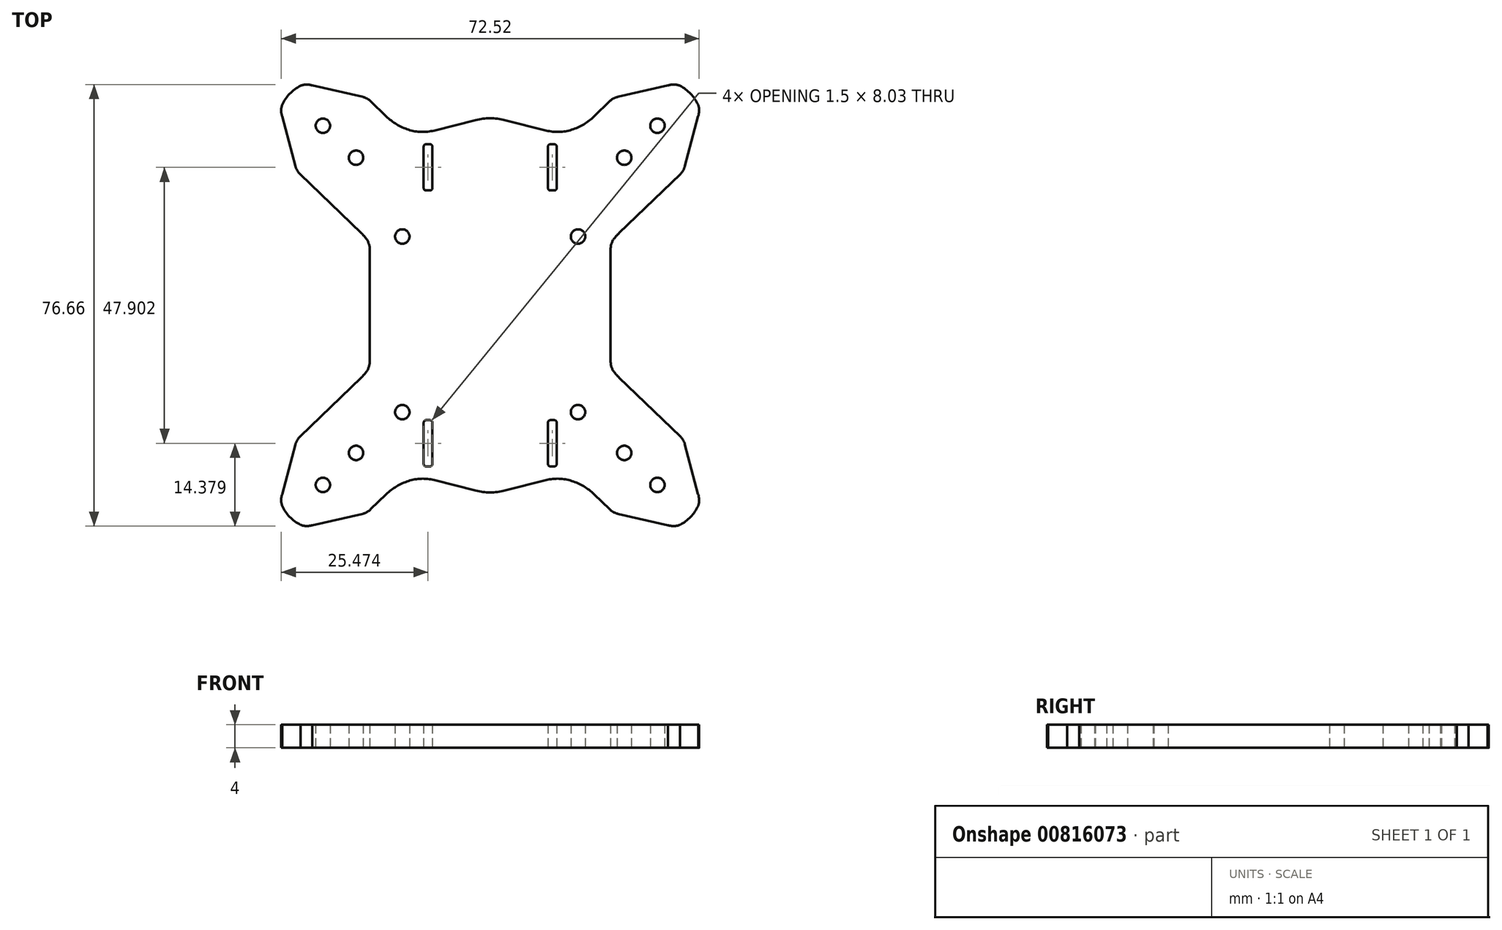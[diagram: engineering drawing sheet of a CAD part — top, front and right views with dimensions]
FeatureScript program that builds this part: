
annotation { "Feature Type Name" : "Feature", "Feature Type Description" : "" }
export const myFeature = defineFeature(function(context is Context, id is Id, definition is map)
    precondition{}
    {
        {
            var Q0;
            Q0=qCreatedBy(makeId("Top.planeOp"),FACE);
            var sketch = newSketch(context, id + "F0", { "sketchPlane" : qUnion([Q0])});
            skArc(sketch, "E0.filletArc", {"start": v(22.37, 12.53) * mm, "mid": v(21.96, 12.11) * mm, "end": v(21.58, 11.68) * mm});
            skArc(sketch, "E1.MirrorCS", {"start": v(18.04, 32.81) * mm, "mid": v(16.23, 31.43) * mm, "end": v(14.16, 30.49) * mm});
            skArc(sketch, "E2.MirrorCS", {"start": v(32.98, 22.77) * mm, "mid": v(33.49, 23.41) * mm, "end": v(33.8, 24.17) * mm});
            skLineSegment(sketch, "E3.MirrorCS", {"start": v(20, 34.7) * mm, "end": v(18.04, 32.81) * mm});
            skLineSegment(sketch, "E4.MirrorCS", {"start": v(20, 34.7) * mm, "end": v(20.76, 35.44) * mm});
            skLineSegment(sketch, "E5.MirrorCS", {"start": v(25.58, 36.97) * mm, "end": v(22.18, 36.2) * mm});
            skArc(sketch, "E6.MirrorCS", {"start": v(36.09, 34.84) * mm, "mid": v(36.26, 33.8) * mm, "end": v(36.07, 32.77) * mm});
            skArc(sketch, "E7.MirrorCS", {"start": v(32.93, 38.11) * mm, "mid": v(31.9, 38.32) * mm, "end": v(30.86, 38.17) * mm});
            skLineSegment(sketch, "E8.MirrorCS", {"start": v(34.69, 27.53) * mm, "end": v(33.8, 24.17) * mm});
            skArc(sketch, "E9.MirrorCS", {"start": v(22.18, 36.2) * mm, "mid": v(21.42, 35.92) * mm, "end": v(20.76, 35.44) * mm});
            skArc(sketch, "E10.MirrorCS", {"start": v(36.09, 34.84) * mm, "mid": v(34.78, 36.74) * mm, "end": v(32.93, 38.11) * mm});
            skLineSegment(sketch, "E11.MirrorCS", {"start": v(30.86, 38.17) * mm, "end": v(25.58, 36.97) * mm});
            skLineSegment(sketch, "E12.MirrorCS", {"start": v(36.07, 32.77) * mm, "end": v(34.69, 27.53) * mm});
            skCircle(sketch, "E13.MirrorC", {"center": v(29.03, 31.18) * mm, "radius": 1.25 * mm});
            skCircle(sketch, "E14.MirrorC", {"center": v(23.27, 25.63) * mm, "radius": 1.25 * mm});
            skLineSegment(sketch, "E15.MirrorCS", {"start": v(32.98, 22.77) * mm, "end": v(22.37, 12.53) * mm});
            skLineSegment(sketch, "E16", {"start": v(2.5, 32.18) * mm, "end": v(9.75, 30.34) * mm});
            skArc(sketch, "E17.filletArc", {"start": v(9.75, 30.34) * mm, "mid": v(11.97, 30.1) * mm, "end": v(14.16, 30.49) * mm});
            skPoint(sketch, "E18.visualSharp", {"position": v(20.83, 7.15) * mm});
            skArc(sketch, "E18.filletArc", {"start": v(21.58, 11.68) * mm, "mid": v(21.08, 10.79) * mm, "end": v(20.9, 9.77) * mm});
            skLineSegment(sketch, "E19.bottom", {"start": v(10.04, 11.8) * mm, "end": v(-8.96, 11.8) * mm, "construction": true});
            skPoint(sketch, "E20", {"position": v(10.04, 24.6) * mm});
            skLineSegment(sketch, "E21.MirrorCS", {"start": v(10.04, 27.56) * mm, "end": v(10.04, 24.6) * mm});
            skLineSegment(sketch, "E22.MirrorCS", {"start": v(10.44, 27.96) * mm, "end": v(11.14, 27.96) * mm});
            skLineSegment(sketch, "E23.MirrorCS", {"start": v(11.54, 27.56) * mm, "end": v(11.54, 20.34) * mm});
            skLineSegment(sketch, "E24.MirrorCS", {"start": v(10.04, 24.6) * mm, "end": v(10.04, 20.34) * mm});
            skLineSegment(sketch, "E25.MirrorCS", {"start": v(10.44, 19.94) * mm, "end": v(11.14, 19.94) * mm});
            skPoint(sketch, "E26.visualSharp", {"position": v(11.54, 16.64) * mm});
            skArc(sketch, "E26.filletArc", {"start": v(11.14, 19.94) * mm, "mid": v(11.42, 20.05) * mm, "end": v(11.54, 20.34) * mm});
            skPoint(sketch, "E27.visualSharp", {"position": v(11.54, 27.96) * mm});
            skArc(sketch, "E27.filletArc", {"start": v(11.54, 27.56) * mm, "mid": v(11.42, 27.85) * mm, "end": v(11.14, 27.96) * mm});
            skPoint(sketch, "E28.visualSharp", {"position": v(10.04, 16.64) * mm});
            skArc(sketch, "E28.filletArc", {"start": v(10.04, 20.34) * mm, "mid": v(10.15, 20.05) * mm, "end": v(10.44, 19.94) * mm});
            skLineSegment(sketch, "E29.trimOffspring", {"start": v(10.04, 30.28) * mm, "end": v(10.04, 34.1) * mm, "construction": true});
            skPoint(sketch, "E30.MirrorCS.start.orphan", {"position": v(10.04, 27.96) * mm});
            skPoint(sketch, "E31.orphan", {"position": v(10.29, 8.83) * mm});
            skArc(sketch, "E32.filletArc", {"start": v(10.44, 27.96) * mm, "mid": v(10.15, 27.85) * mm, "end": v(10.04, 27.56) * mm});
            skLineSegment(sketch, "E33.MirrorCS", {"start": v(-10.44, 27.96) * mm, "end": v(-11.14, 27.96) * mm});
            skArc(sketch, "E34.MirrorCS", {"start": v(-11.54, 27.56) * mm, "mid": v(-11.42, 27.85) * mm, "end": v(-11.14, 27.96) * mm});
            skArc(sketch, "E35.MirrorCS", {"start": v(-10.44, 27.96) * mm, "mid": v(-10.15, 27.85) * mm, "end": v(-10.04, 27.56) * mm});
            skLineSegment(sketch, "E36.MirrorCS", {"start": v(-10.44, 19.94) * mm, "end": v(-11.14, 19.94) * mm});
            skArc(sketch, "E37.MirrorCS", {"start": v(-11.14, 19.94) * mm, "mid": v(-11.42, 20.05) * mm, "end": v(-11.54, 20.34) * mm});
            skArc(sketch, "E38.MirrorCS", {"start": v(-10.04, 20.34) * mm, "mid": v(-10.15, 20.05) * mm, "end": v(-10.44, 19.94) * mm});
            skLineSegment(sketch, "E39.MirrorCS", {"start": v(-10.04, 27.56) * mm, "end": v(-10.04, 24.6) * mm});
            skLineSegment(sketch, "E40.MirrorCS", {"start": v(-11.54, 27.56) * mm, "end": v(-11.54, 20.34) * mm});
            skLineSegment(sketch, "E41.MirrorCS", {"start": v(-10.04, 24.6) * mm, "end": v(-10.04, 20.34) * mm});
            skLineSegment(sketch, "E42.MirrorCS", {"start": v(-20, 34.7) * mm, "end": v(-18.04, 32.81) * mm});
            skLineSegment(sketch, "E43.MirrorCS", {"start": v(-34.69, 27.53) * mm, "end": v(-33.8, 24.17) * mm});
            skArc(sketch, "E44.MirrorCS", {"start": v(-32.98, 22.77) * mm, "mid": v(-33.49, 23.41) * mm, "end": v(-33.8, 24.17) * mm});
            skArc(sketch, "E45.MirrorCS", {"start": v(-9.75, 30.34) * mm, "mid": v(-11.97, 30.1) * mm, "end": v(-14.16, 30.49) * mm});
            skLineSegment(sketch, "E46.MirrorCS", {"start": v(-25.58, 36.97) * mm, "end": v(-22.18, 36.2) * mm});
            skArc(sketch, "E47.MirrorCS", {"start": v(-22.18, 36.2) * mm, "mid": v(-21.42, 35.92) * mm, "end": v(-20.76, 35.44) * mm});
            skArc(sketch, "E48.MirrorCS", {"start": v(-22.37, 12.53) * mm, "mid": v(-21.96, 12.11) * mm, "end": v(-21.58, 11.68) * mm});
            skArc(sketch, "E49.MirrorCS", {"start": v(-32.93, 38.11) * mm, "mid": v(-31.9, 38.32) * mm, "end": v(-30.86, 38.17) * mm});
            skArc(sketch, "E50.MirrorCS", {"start": v(-36.09, 34.84) * mm, "mid": v(-36.26, 33.8) * mm, "end": v(-36.07, 32.77) * mm});
            skPoint(sketch, "E51.MirrorP", {"position": v(-10.04, 24.6) * mm});
            skLineSegment(sketch, "E52.MirrorCS", {"start": v(-20, 34.7) * mm, "end": v(-20.76, 35.44) * mm});
            skArc(sketch, "E53.MirrorCS", {"start": v(-36.09, 34.84) * mm, "mid": v(-34.78, 36.74) * mm, "end": v(-32.93, 38.11) * mm});
            skArc(sketch, "E54.MirrorCS", {"start": v(-18.04, 32.81) * mm, "mid": v(-16.23, 31.43) * mm, "end": v(-14.16, 30.49) * mm});
            skArc(sketch, "E55.MirrorCS", {"start": v(-21.58, 11.68) * mm, "mid": v(-21.08, 10.79) * mm, "end": v(-20.9, 9.77) * mm});
            skLineSegment(sketch, "E56.MirrorCS", {"start": v(-36.07, 32.77) * mm, "end": v(-34.69, 27.53) * mm});
            skCircle(sketch, "E57.MirrorC", {"center": v(-29.03, 31.18) * mm, "radius": 1.25 * mm});
            skPoint(sketch, "E58.MirrorP", {"position": v(-10.04, 27.96) * mm});
            skLineSegment(sketch, "E59.MirrorCS", {"start": v(-10.04, 30.28) * mm, "end": v(-10.04, 34.1) * mm, "construction": true});
            skLineSegment(sketch, "E60.MirrorCS", {"start": v(-32.98, 22.77) * mm, "end": v(-22.37, 12.53) * mm});
            skPoint(sketch, "E61.MirrorP", {"position": v(-11.54, 27.96) * mm});
            skLineSegment(sketch, "E62.MirrorCS", {"start": v(-2.5, 32.18) * mm, "end": v(-9.75, 30.34) * mm});
            skCircle(sketch, "E63.MirrorC", {"center": v(-23.27, 25.63) * mm, "radius": 1.25 * mm});
            skPoint(sketch, "E64.MirrorP", {"position": v(-10.29, 8.83) * mm});
            skPoint(sketch, "E65.MirrorP", {"position": v(-10.04, 16.64) * mm});
            skPoint(sketch, "E66.MirrorP", {"position": v(-11.54, 16.64) * mm});
            skLineSegment(sketch, "E67.MirrorCS", {"start": v(-30.86, 38.17) * mm, "end": v(-25.58, 36.97) * mm});
            skPoint(sketch, "E68.MirrorP", {"position": v(-19.3, 4.04) * mm});
            skArc(sketch, "E69", {"start": v(2.5, 32.18) * mm, "mid": v(0, 32.49) * mm, "end": v(-2.5, 32.18) * mm});
            skArc(sketch, "E70.MirrorCS", {"start": v(11.54, -27.56) * mm, "mid": v(11.42, -27.85) * mm, "end": v(11.14, -27.96) * mm});
            skArc(sketch, "E71.MirrorCS", {"start": v(10.44, -27.96) * mm, "mid": v(10.15, -27.85) * mm, "end": v(10.04, -27.56) * mm});
            skLineSegment(sketch, "E72.MirrorCS", {"start": v(10.44, -27.96) * mm, "end": v(11.14, -27.96) * mm});
            skArc(sketch, "E73.MirrorCS", {"start": v(10.04, -20.34) * mm, "mid": v(10.15, -20.05) * mm, "end": v(10.44, -19.94) * mm});
            skLineSegment(sketch, "E74.MirrorCS", {"start": v(10.04, -27.56) * mm, "end": v(10.04, -24.6) * mm});
            skArc(sketch, "E75.MirrorCS", {"start": v(-10.04, -20.34) * mm, "mid": v(-10.15, -20.05) * mm, "end": v(-10.44, -19.94) * mm});
            skArc(sketch, "E76.MirrorCS", {"start": v(11.14, -19.94) * mm, "mid": v(11.42, -20.05) * mm, "end": v(11.54, -20.34) * mm});
            skArc(sketch, "E77.MirrorCS", {"start": v(-10.44, -27.96) * mm, "mid": v(-10.15, -27.85) * mm, "end": v(-10.04, -27.56) * mm});
            skLineSegment(sketch, "E78.MirrorCS", {"start": v(10.44, -19.94) * mm, "end": v(11.14, -19.94) * mm});
            skLineSegment(sketch, "E79.MirrorCS", {"start": v(-10.04, -27.56) * mm, "end": v(-10.04, -24.6) * mm});
            skArc(sketch, "E80.MirrorCS", {"start": v(-11.14, -19.94) * mm, "mid": v(-11.42, -20.05) * mm, "end": v(-11.54, -20.34) * mm});
            skLineSegment(sketch, "E81.MirrorCS", {"start": v(-10.04, -24.6) * mm, "end": v(-10.04, -20.34) * mm});
            skLineSegment(sketch, "E82.MirrorCS", {"start": v(-10.44, -27.96) * mm, "end": v(-11.14, -27.96) * mm});
            skLineSegment(sketch, "E83.MirrorCS", {"start": v(10.04, -24.6) * mm, "end": v(10.04, -20.34) * mm});
            skArc(sketch, "E84.MirrorCS", {"start": v(-11.54, -27.56) * mm, "mid": v(-11.42, -27.85) * mm, "end": v(-11.14, -27.96) * mm});
            skLineSegment(sketch, "E85.MirrorCS", {"start": v(-11.54, -27.56) * mm, "end": v(-11.54, -20.34) * mm});
            skLineSegment(sketch, "E86.MirrorCS", {"start": v(-10.44, -19.94) * mm, "end": v(-11.14, -19.94) * mm});
            skLineSegment(sketch, "E87.MirrorCS", {"start": v(11.54, -27.56) * mm, "end": v(11.54, -20.34) * mm});
            skArc(sketch, "E88.MirrorCS", {"start": v(32.93, -38.11) * mm, "mid": v(31.9, -38.32) * mm, "end": v(30.86, -38.17) * mm});
            skLineSegment(sketch, "E89.MirrorCS", {"start": v(25.58, -36.97) * mm, "end": v(22.18, -36.2) * mm});
            skPoint(sketch, "E90.MirrorP", {"position": v(-10.04, -24.6) * mm});
            skArc(sketch, "E91.MirrorCS", {"start": v(-9.75, -30.34) * mm, "mid": v(-11.97, -30.1) * mm, "end": v(-14.16, -30.49) * mm});
            skArc(sketch, "E92.MirrorCS", {"start": v(18.04, -32.81) * mm, "mid": v(16.23, -31.43) * mm, "end": v(14.16, -30.49) * mm});
            skArc(sketch, "E93.MirrorCS", {"start": v(22.18, -36.2) * mm, "mid": v(21.42, -35.92) * mm, "end": v(20.76, -35.44) * mm});
            skLineSegment(sketch, "E94.MirrorCS", {"start": v(30.86, -38.17) * mm, "end": v(25.58, -36.97) * mm});
            skArc(sketch, "E95.MirrorCS", {"start": v(9.75, -30.34) * mm, "mid": v(11.97, -30.1) * mm, "end": v(14.16, -30.49) * mm});
            skLineSegment(sketch, "E96.MirrorCS", {"start": v(-20, -34.7) * mm, "end": v(-20.76, -35.44) * mm});
            skLineSegment(sketch, "E97.MirrorCS", {"start": v(-20, -34.7) * mm, "end": v(-18.04, -32.81) * mm});
            skLineSegment(sketch, "E98.MirrorCS", {"start": v(-25.58, -36.97) * mm, "end": v(-22.18, -36.2) * mm});
            skArc(sketch, "E99.MirrorCS", {"start": v(-21.58, -11.68) * mm, "mid": v(-21.08, -10.79) * mm, "end": v(-20.9, -9.77) * mm});
            skArc(sketch, "E100.MirrorCS", {"start": v(-22.18, -36.2) * mm, "mid": v(-21.42, -35.92) * mm, "end": v(-20.76, -35.44) * mm});
            skArc(sketch, "E101.MirrorCS", {"start": v(36.09, -34.84) * mm, "mid": v(36.26, -33.8) * mm, "end": v(36.07, -32.77) * mm});
            skArc(sketch, "E102.MirrorCS", {"start": v(22.37, -12.53) * mm, "mid": v(21.96, -12.11) * mm, "end": v(21.58, -11.68) * mm});
            skArc(sketch, "E103.MirrorCS", {"start": v(-36.09, -34.84) * mm, "mid": v(-34.78, -36.74) * mm, "end": v(-32.93, -38.11) * mm});
            skPoint(sketch, "E104.MirrorP", {"position": v(10.04, -24.6) * mm});
            skLineSegment(sketch, "E105.MirrorCS", {"start": v(-34.69, -27.53) * mm, "end": v(-33.8, -24.17) * mm});
            skArc(sketch, "E106.MirrorCS", {"start": v(-32.98, -22.77) * mm, "mid": v(-33.49, -23.41) * mm, "end": v(-33.8, -24.17) * mm});
            skArc(sketch, "E107.MirrorCS", {"start": v(-22.37, -12.53) * mm, "mid": v(-21.96, -12.11) * mm, "end": v(-21.58, -11.68) * mm});
            skArc(sketch, "E108.MirrorCS", {"start": v(36.09, -34.84) * mm, "mid": v(34.78, -36.74) * mm, "end": v(32.93, -38.11) * mm});
            skLineSegment(sketch, "E109.MirrorCS", {"start": v(20, -34.7) * mm, "end": v(18.04, -32.81) * mm});
            skArc(sketch, "E110.MirrorCS", {"start": v(21.58, -11.68) * mm, "mid": v(21.08, -10.79) * mm, "end": v(20.9, -9.77) * mm});
            skLineSegment(sketch, "E111.MirrorCS", {"start": v(20, -34.7) * mm, "end": v(20.76, -35.44) * mm});
            skArc(sketch, "E112.MirrorCS", {"start": v(32.98, -22.77) * mm, "mid": v(33.49, -23.41) * mm, "end": v(33.8, -24.17) * mm});
            skArc(sketch, "E113.MirrorCS", {"start": v(-18.04, -32.81) * mm, "mid": v(-16.23, -31.43) * mm, "end": v(-14.16, -30.49) * mm});
            skArc(sketch, "E114.MirrorCS", {"start": v(-32.93, -38.11) * mm, "mid": v(-31.9, -38.32) * mm, "end": v(-30.86, -38.17) * mm});
            skArc(sketch, "E115.MirrorCS", {"start": v(-36.09, -34.84) * mm, "mid": v(-36.26, -33.8) * mm, "end": v(-36.07, -32.77) * mm});
            skLineSegment(sketch, "E116.MirrorCS", {"start": v(34.69, -27.53) * mm, "end": v(33.8, -24.17) * mm});
            skLineSegment(sketch, "E117.MirrorCS", {"start": v(10.04, -30.28) * mm, "end": v(10.04, -34.1) * mm, "construction": true});
            skPoint(sketch, "E118.MirrorP", {"position": v(10.04, -27.96) * mm});
            skLineSegment(sketch, "E119.MirrorCS", {"start": v(-10.04, -30.28) * mm, "end": v(-10.04, -34.1) * mm, "construction": true});
            skPoint(sketch, "E120.MirrorP", {"position": v(-10.04, -27.96) * mm});
            skLineSegment(sketch, "E121.MirrorCS", {"start": v(-36.07, -32.77) * mm, "end": v(-34.69, -27.53) * mm});
            skPoint(sketch, "E122.MirrorP", {"position": v(11.54, -19.94) * mm});
            skPoint(sketch, "E123.MirrorP", {"position": v(-10.04, -19.94) * mm});
            skLineSegment(sketch, "E124.MirrorCS", {"start": v(36.07, -32.77) * mm, "end": v(34.69, -27.53) * mm});
            skPoint(sketch, "E125.MirrorP", {"position": v(-11.54, -19.94) * mm});
            skPoint(sketch, "E126.MirrorP", {"position": v(-20.83, -7.15) * mm});
            skArc(sketch, "E127.MirrorCS", {"start": v(2.5, -32.18) * mm, "mid": v(0, -32.49) * mm, "end": v(-2.5, -32.18) * mm});
            skLineSegment(sketch, "E128.MirrorCS", {"start": v(-30.86, -38.17) * mm, "end": v(-25.58, -36.97) * mm});
            skLineSegment(sketch, "E129.MirrorCS", {"start": v(-32.98, -22.77) * mm, "end": v(-22.37, -12.53) * mm});
            skPoint(sketch, "E130.MirrorP", {"position": v(-11.54, -27.96) * mm});
            skLineSegment(sketch, "E131.MirrorCS", {"start": v(10.04, -18.4) * mm, "end": v(-8.96, -18.4) * mm, "construction": true});
            skLineSegment(sketch, "E132.MirrorCS", {"start": v(-2.5, -32.18) * mm, "end": v(-9.75, -30.34) * mm});
            skPoint(sketch, "E133.MirrorP", {"position": v(19.3, -10.64) * mm});
            skLineSegment(sketch, "E134.MirrorCS", {"start": v(32.98, -22.77) * mm, "end": v(22.37, -12.53) * mm});
            skCircle(sketch, "E135.MirrorC", {"center": v(-23.27, -25.63) * mm, "radius": 1.25 * mm});
            skLineSegment(sketch, "E136.MirrorCS", {"start": v(2.5, -32.18) * mm, "end": v(9.75, -30.34) * mm});
            skCircle(sketch, "E137.MirrorC", {"center": v(23.27, -25.63) * mm, "radius": 1.25 * mm});
            skCircle(sketch, "E138.MirrorC", {"center": v(-29.03, -31.18) * mm, "radius": 1.25 * mm});
            skPoint(sketch, "E139.MirrorP", {"position": v(10.04, -19.94) * mm});
            skCircle(sketch, "E140.MirrorC", {"center": v(29.03, -31.18) * mm, "radius": 1.25 * mm});
            skPoint(sketch, "E141.MirrorP", {"position": v(11.54, -27.96) * mm});
            skLineSegment(sketch, "E142", {"start": v(-20.9, 9.77) * mm, "end": v(-20.9, -9.77) * mm});
            skLineSegment(sketch, "E143", {"start": v(20.9, 9.77) * mm, "end": v(20.9, -9.77) * mm});
            skLineSegment(sketch, "E144.bottom", {"start": v(15.25, -18.55) * mm, "end": v(-15.25, -18.55) * mm, "construction": true});
            skLineSegment(sketch, "E144.top", {"start": v(15.25, 11.95) * mm, "end": v(-15.25, 11.95) * mm, "construction": true});
            skLineSegment(sketch, "E144.left", {"start": v(15.25, -18.55) * mm, "end": v(15.25, 11.95) * mm, "construction": true});
            skLineSegment(sketch, "E144.right", {"start": v(-15.25, -18.55) * mm, "end": v(-15.25, 11.95) * mm, "construction": true});
            skPoint(sketch, "E144.middle", {"position": v(0, -3.3) * mm});
            skCircle(sketch, "E145", {"center": v(-15.25, 11.95) * mm, "radius": 1.25 * mm});
            skCircle(sketch, "E146", {"center": v(15.25, 11.95) * mm, "radius": 1.25 * mm});
            skCircle(sketch, "E147", {"center": v(15.25, -18.55) * mm, "radius": 1.25 * mm});
            skCircle(sketch, "E148", {"center": v(-15.25, -18.55) * mm, "radius": 1.25 * mm});
            skSolve(sketch);
        }
        {
            var Q0;
            Q0 = qSketchRegion(id + "F0", true);
            extrude(context, id + "F1", {"entities" : qUnion([Q0]), "depth" : 4 * mm, "offsetDistance" : 25 * mm});
        }
    });
